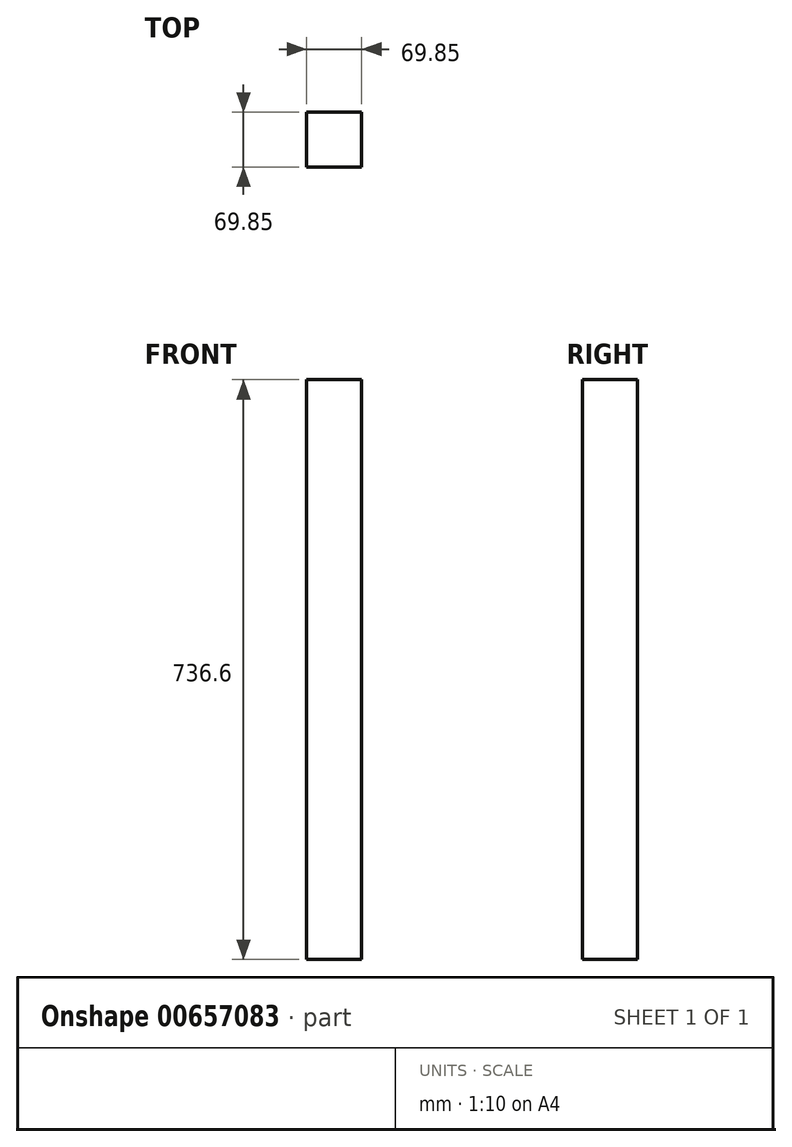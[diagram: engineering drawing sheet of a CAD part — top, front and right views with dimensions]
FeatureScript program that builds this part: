
annotation { "Feature Type Name" : "Feature", "Feature Type Description" : "" }
export const myFeature = defineFeature(function(context is Context, id is Id, definition is map)
    precondition{}
    {
        {
            var Q0;
            Q0=qCreatedBy(makeId("Top.planeOp"),FACE);
            var sketch = newSketch(context, id + "F0", { "sketchPlane" : qUnion([Q0])});
            skLineSegment(sketch, "E0.bottom", {"start": v(-85.78, -7.63) * mm, "end": v(-15.93, -7.63) * mm});
            skLineSegment(sketch, "E0.top", {"start": v(-85.78, -77.48) * mm, "end": v(-15.93, -77.48) * mm});
            skLineSegment(sketch, "E0.left", {"start": v(-85.78, -7.63) * mm, "end": v(-85.78, -77.48) * mm});
            skLineSegment(sketch, "E0.right", {"start": v(-15.93, -7.63) * mm, "end": v(-15.93, -77.48) * mm});
            skSolve(sketch);
        }
        {
            var Q0;
            Q0 = qSketchRegion(id + "F0", true);
            extrude(context, id + "F1", {"entities" : qUnion([Q0]), "depth" : 736.6 * mm, "offsetDistance" : 25.4 * mm});
        }
    });
